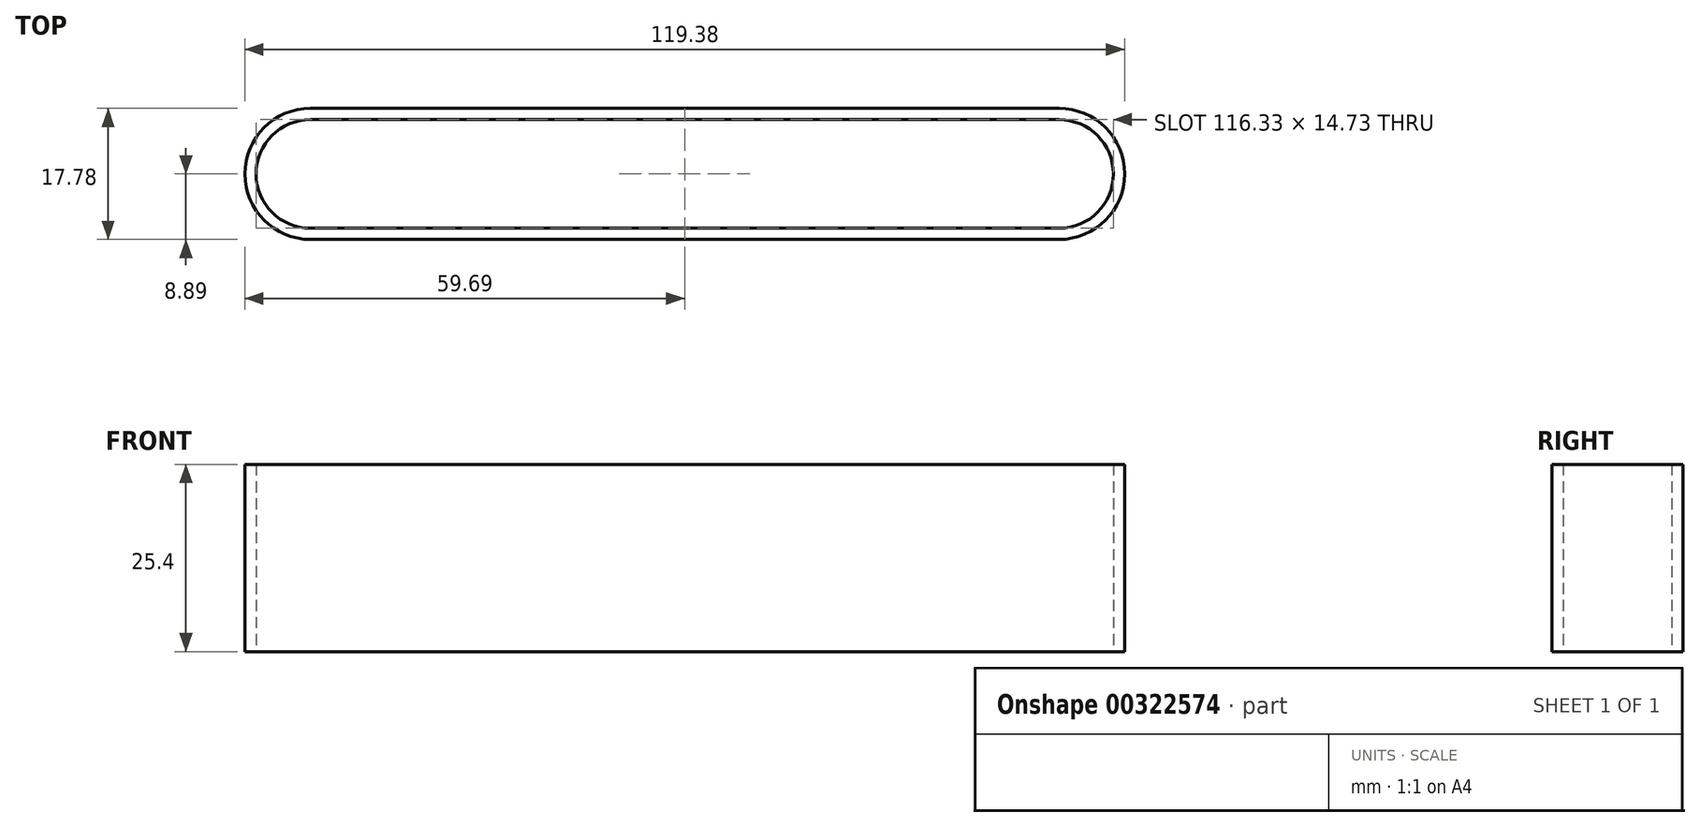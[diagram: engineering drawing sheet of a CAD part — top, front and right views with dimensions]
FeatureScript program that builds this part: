
annotation { "Feature Type Name" : "Feature", "Feature Type Description" : "" }
export const myFeature = defineFeature(function(context is Context, id is Id, definition is map)
    precondition{}
    {
        {
            var Q0;
            Q0=qCreatedBy(makeId("Top.planeOp"),FACE);
            var sketch = newSketch(context, id + "F0", { "sketchPlane" : qUnion([Q0])});
            skArc(sketch, "E0", {"start": v(0, 8.9) * mm, "mid": v(-8.9, 0) * mm, "end": v(0, -8.9) * mm});
            skArc(sketch, "E1", {"start": v(101.6, -8.9) * mm, "mid": v(110.5, 0) * mm, "end": v(101.6, 8.89) * mm});
            skLineSegment(sketch, "E2", {"start": v(0, 8.9) * mm, "end": v(101.6, 8.89) * mm});
            skLineSegment(sketch, "E3", {"start": v(0, -8.9) * mm, "end": v(101.6, -8.9) * mm});
            skLineSegment(sketch, "E4.0", {"start": v(0, -7.37) * mm, "end": v(101.6, -7.37) * mm});
            skArc(sketch, "E4.1", {"start": v(0, 7.37) * mm, "mid": v(-7.37, 0) * mm, "end": v(0, -7.37) * mm});
            skLineSegment(sketch, "E4.2", {"start": v(0, 7.37) * mm, "end": v(101.6, 7.37) * mm});
            skArc(sketch, "E4.3", {"start": v(101.6, -7.37) * mm, "mid": v(108.97, 0) * mm, "end": v(101.6, 7.37) * mm});
            skSolve(sketch);
        }
        {
            var Q0;
            Q0 = qSketchRegion(id + "F0", true);
            extrude(context, id + "F1", {"entities" : qUnion([Q0]), "depth" : 25.4 * mm, "offsetDistance" : 25.4 * mm});
        }
    });
